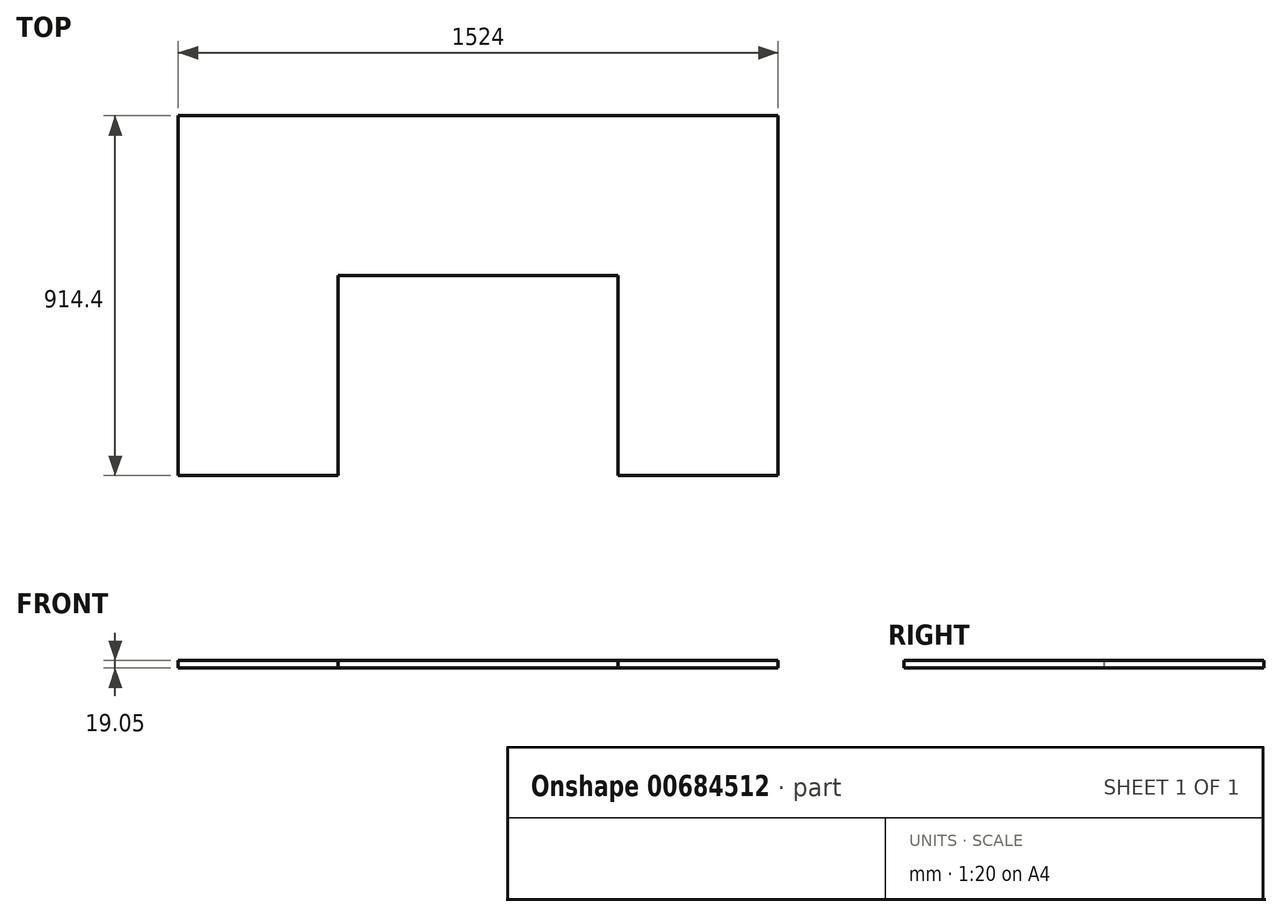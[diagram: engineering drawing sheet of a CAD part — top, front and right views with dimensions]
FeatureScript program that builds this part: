
annotation { "Feature Type Name" : "Feature", "Feature Type Description" : "" }
export const myFeature = defineFeature(function(context is Context, id is Id, definition is map)
    precondition{}
    {
        {
            var Q0;
            Q0=qCreatedBy(makeId("Top.planeOp"),FACE);
            var sketch = newSketch(context, id + "F0", { "sketchPlane" : qUnion([Q0])});
            skLineSegment(sketch, "E0", {"start": v(-729.36, -456.62) * mm, "end": v(-729.36, 457.78) * mm});
            skLineSegment(sketch, "E1", {"start": v(-729.36, 457.78) * mm, "end": v(794.64, 457.78) * mm});
            skLineSegment(sketch, "E2", {"start": v(794.64, 457.78) * mm, "end": v(794.64, -456.62) * mm});
            skLineSegment(sketch, "E3", {"start": v(794.64, -456.62) * mm, "end": v(388.24, -456.62) * mm});
            skLineSegment(sketch, "E4", {"start": v(388.24, -456.62) * mm, "end": v(388.24, 51.38) * mm});
            skLineSegment(sketch, "E5", {"start": v(388.24, 51.38) * mm, "end": v(-322.96, 51.38) * mm});
            skLineSegment(sketch, "E6", {"start": v(-322.96, 51.38) * mm, "end": v(-322.96, -456.62) * mm});
            skLineSegment(sketch, "E7", {"start": v(-322.96, -456.62) * mm, "end": v(-729.36, -456.62) * mm});
            skSolve(sketch);
        }
        {
            var Q0;
            Q0=makeQuery(id+"F0.imprint","IMPRINT",FACE,{"disambiguationData":[TD([[makeQuery(id+"F0.imprint","IMPRINT",EDGE,{"derivedFrom":sQuery(id+"F0.wireOp",EDGE,"E0")}),-1.0]])]});
            extrude(context, id + "F1", {"entities" : qUnion([Q0]), "depth" : 19.05 * mm, "offsetDistance" : 25.4 * mm});
        }
    });
